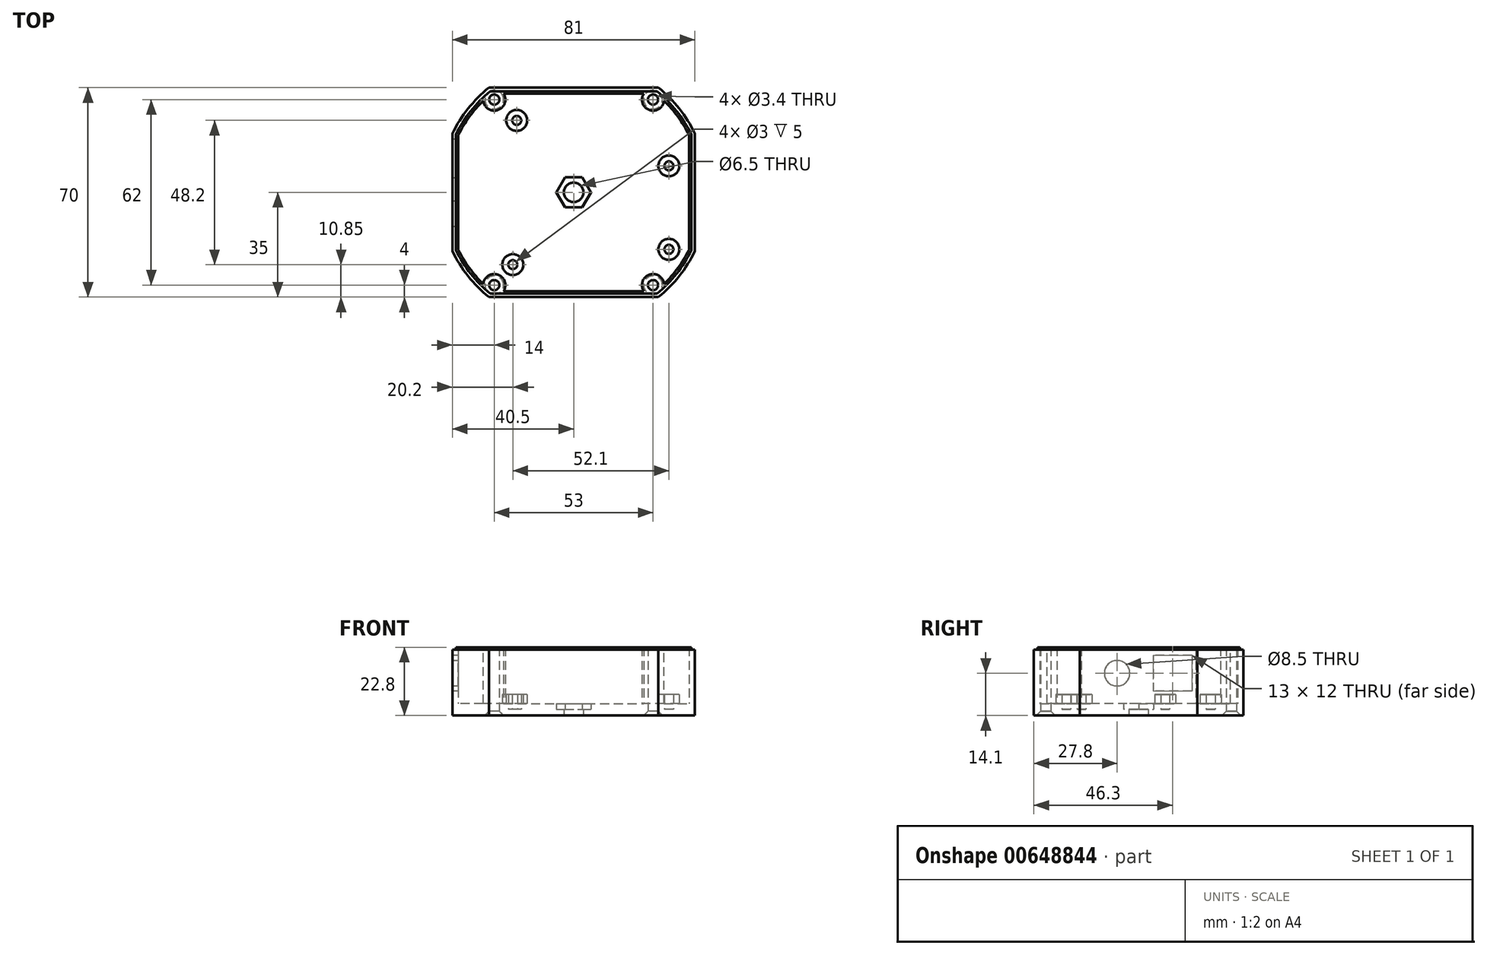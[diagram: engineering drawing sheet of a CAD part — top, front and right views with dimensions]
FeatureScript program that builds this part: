
annotation { "Feature Type Name" : "Feature", "Feature Type Description" : "" }
export const myFeature = defineFeature(function(context is Context, id is Id, definition is map)
    precondition{}
    {
        {
            var Q0;
            Q0=qCreatedBy(makeId("Top.planeOp"),FACE);
            var sketch = newSketch(context, id + "F0", { "sketchPlane" : qUnion([Q0])});
            skArc(sketch, "E0", {"start": v(-40.5, -19.62) * mm, "mid": v(-35.24, -27.98) * mm, "end": v(-28.28, -35) * mm});
            skLineSegment(sketch, "E1", {"start": v(-40.5, 19.62) * mm, "end": v(-40.5, -19.62) * mm});
            skLineSegment(sketch, "E2", {"start": v(-28.28, -35) * mm, "end": v(28.28, -35) * mm});
            skLineSegment(sketch, "E3", {"start": v(-28.28, 35) * mm, "end": v(28.28, 35) * mm});
            skArc(sketch, "E4.trimOffspring", {"start": v(-28.28, 35) * mm, "mid": v(-35.24, 27.98) * mm, "end": v(-40.5, 19.62) * mm});
            skArc(sketch, "E5.trimOffspring", {"start": v(28.28, -35) * mm, "mid": v(35.24, -27.98) * mm, "end": v(40.5, -19.62) * mm});
            skLineSegment(sketch, "E6", {"start": v(40.5, 19.62) * mm, "end": v(40.5, -19.62) * mm});
            skArc(sketch, "E7.trimOffspring", {"start": v(40.5, 19.62) * mm, "mid": v(35.24, 27.98) * mm, "end": v(28.28, 35) * mm});
            skLineSegment(sketch, "E8.bottom", {"start": v(34.3, 26.65) * mm, "end": v(-34.3, 26.65) * mm, "construction": true});
            skLineSegment(sketch, "E8.top", {"start": v(34.3, -26.65) * mm, "end": v(-34.3, -26.65) * mm, "construction": true});
            skLineSegment(sketch, "E8.left", {"start": v(34.3, 26.65) * mm, "end": v(34.3, -26.65) * mm, "construction": true});
            skLineSegment(sketch, "E8.right", {"start": v(-34.3, 26.65) * mm, "end": v(-34.3, -26.65) * mm, "construction": true});
            skLineSegment(sketch, "E9.bottom", {"start": v(-40.5, 17.05) * mm, "end": v(-34.3, 17.05) * mm, "construction": true});
            skLineSegment(sketch, "E9.top", {"start": v(-40.5, 5.05) * mm, "end": v(-34.3, 5.05) * mm, "construction": true});
            skLineSegment(sketch, "E9.left", {"start": v(-40.5, 17.05) * mm, "end": v(-40.5, 5.05) * mm, "construction": true});
            skLineSegment(sketch, "E9.right", {"start": v(-34.3, 17.05) * mm, "end": v(-34.3, 5.05) * mm, "construction": true});
            skPoint(sketch, "E10", {"position": v(-26.5, 31) * mm});
            skPoint(sketch, "E11", {"position": v(26.5, 31) * mm});
            skPoint(sketch, "E12", {"position": v(-26.5, -31) * mm});
            skPoint(sketch, "E13", {"position": v(26.5, -31) * mm});
            skCircle(sketch, "E14", {"center": v(-26.5, 31) * mm, "radius": 1.7 * mm});
            skCircle(sketch, "E15", {"center": v(26.5, 31) * mm, "radius": 1.7 * mm});
            skCircle(sketch, "E16", {"center": v(26.5, -31) * mm, "radius": 1.7 * mm});
            skCircle(sketch, "E17", {"center": v(-26.5, -31) * mm, "radius": 1.7 * mm});
            skPoint(sketch, "E18", {"position": v(-19, 24.05) * mm});
            skPoint(sketch, "E19", {"position": v(31.8, 8.85) * mm});
            skPoint(sketch, "E20", {"position": v(-20.3, -24.15) * mm});
            skPoint(sketch, "E21", {"position": v(31.8, -19.05) * mm});
            skSolve(sketch);
        }
        {
            var Q0;
            Q0=makeQuery(id+"F0.imprint","IMPRINT",FACE,{"disambiguationData":[TD([[makeQuery(id+"F0.imprint","IMPRINT",EDGE,{"derivedFrom":sQuery(id+"F0.wireOp",EDGE,"E0")}),1.0]])]});
            extrude(context, id + "F1", {"entities" : qUnion([Q0]), "depth" : 22 * mm, "offsetDistance" : 25 * mm});
        }
        {
            var Q0;
            Q0=makeQuery(id+"F1.opExtrude","CAP_FACE",FACE,{"disambiguationData":[OSD([sQuery(id+"F0.wireOp",EDGE,"E0"),sQuery(id+"F0.wireOp",EDGE,"E1"),sQuery(id+"F0.wireOp",EDGE,"E2"),sQuery(id+"F0.wireOp",EDGE,"E3"),sQuery(id+"F0.wireOp",EDGE,"E4.trimOffspring"),sQuery(id+"F0.wireOp",EDGE,"E5.trimOffspring"),sQuery(id+"F0.wireOp",EDGE,"E6"),sQuery(id+"F0.wireOp",EDGE,"E7.trimOffspring")])],"isStart":false});
            shell(context, id + "F2", {"entities" : qUnion([Q0]), "thickness" : 2 * mm});
        }
        {
            var Q0;
            Q0=makeQuery(id+"F1.opExtrude","CAP_EDGE",EDGE,{"disambiguationData":[OSD([sQuery(id+"F0.wireOp",EDGE,"E17")])],"isStart":true});
            var Q1;
            Q1=makeQuery(id+"F1.opExtrude","CAP_EDGE",EDGE,{"disambiguationData":[OSD([sQuery(id+"F0.wireOp",EDGE,"E16")])],"isStart":true});
            var Q2;
            Q2=makeQuery(id+"F1.opExtrude","CAP_EDGE",EDGE,{"disambiguationData":[OSD([sQuery(id+"F0.wireOp",EDGE,"E15")])],"isStart":true});
            var Q3;
            Q3=makeQuery(id+"F1.opExtrude","CAP_EDGE",EDGE,{"disambiguationData":[OSD([sQuery(id+"F0.wireOp",EDGE,"E14")])],"isStart":true});
            chamfer(context, id + "F3", {"entities" : qUnion([Q0, Q1, Q2, Q3]), "width" : 1.4 * mm, "tangentPropagation" : true});
        }
        {
            var Q0;
            Q0=makeQuery(id+"F1.opExtrude","CAP_FACE",FACE,{"disambiguationData":[OSD([sQuery(id+"F0.wireOp",EDGE,"E0"),sQuery(id+"F0.wireOp",EDGE,"E1"),sQuery(id+"F0.wireOp",EDGE,"E2"),sQuery(id+"F0.wireOp",EDGE,"E3"),sQuery(id+"F0.wireOp",EDGE,"E4.trimOffspring"),sQuery(id+"F0.wireOp",EDGE,"E5.trimOffspring"),sQuery(id+"F0.wireOp",EDGE,"E6"),sQuery(id+"F0.wireOp",EDGE,"E7.trimOffspring"),sQuery(id+"F0.wireOp",EDGE,"E14"),sQuery(id+"F0.wireOp",EDGE,"E15"),sQuery(id+"F0.wireOp",EDGE,"E16"),sQuery(id+"F0.wireOp",EDGE,"E17")])],"isStart":false});
            var sketch = newSketch(context, id + "F4", { "sketchPlane" : qUnion([Q0])});
            skLineSegment(sketch, "E22.0", {"start": v(-27.86, 33.8) * mm, "end": v(27.86, 33.8) * mm});
            skArc(sketch, "E22.1", {"start": v(39.3, 19.34) * mm, "mid": v(34.35, 27.18) * mm, "end": v(27.86, 33.8) * mm});
            skArc(sketch, "E22.2", {"start": v(-27.86, 33.8) * mm, "mid": v(-34.35, 27.18) * mm, "end": v(-39.3, 19.34) * mm});
            skLineSegment(sketch, "E22.3", {"start": v(39.3, 19.34) * mm, "end": v(39.3, -19.34) * mm});
            skLineSegment(sketch, "E22.4", {"start": v(-39.3, 19.34) * mm, "end": v(-39.3, -19.34) * mm});
            skArc(sketch, "E22.5", {"start": v(-39.3, -19.34) * mm, "mid": v(-34.35, -27.18) * mm, "end": v(-27.86, -33.8) * mm});
            skLineSegment(sketch, "E22.6", {"start": v(-27.86, -33.8) * mm, "end": v(27.86, -33.8) * mm});
            skArc(sketch, "E22.7", {"start": v(27.86, -33.8) * mm, "mid": v(34.35, -27.18) * mm, "end": v(39.3, -19.34) * mm});
            skSolve(sketch);
        }
        {
            var Q0;
            Q0=makeQuery(id+"F4.imprint","IMPRINT",FACE,{"disambiguationData":[TD([[makeQuery(id+"F4.imprint","IMPRINT",EDGE,{"derivedFrom":sQuery(id+"F4.wireOp",EDGE,"E22.0")}),-1.0]])]});
            extrude(context, id + "F5", {"entities" : qUnion([Q0]), "operationType" : NewBodyOperationType.ADD, "depth" : 0.8 * mm, "offsetDistance" : 25 * mm});
        }
        {
            var Q0;
            Q0=makeQuery(id+"F2.opShell","OFFSET_FACE",FACE,{"disambiguationData":[OSD([sQuery(id+"F0.wireOp",EDGE,"E0"),sQuery(id+"F0.wireOp",EDGE,"E1"),sQuery(id+"F0.wireOp",EDGE,"E2"),sQuery(id+"F0.wireOp",EDGE,"E3"),sQuery(id+"F0.wireOp",EDGE,"E4.trimOffspring"),sQuery(id+"F0.wireOp",EDGE,"E5.trimOffspring"),sQuery(id+"F0.wireOp",EDGE,"E6"),sQuery(id+"F0.wireOp",EDGE,"E7.trimOffspring"),sQuery(id+"F0.wireOp",EDGE,"E14"),sQuery(id+"F0.wireOp",EDGE,"E15"),sQuery(id+"F0.wireOp",EDGE,"E16"),sQuery(id+"F0.wireOp",EDGE,"E17")])]});
            var sketch = newSketch(context, id + "F6", { "sketchPlane" : qUnion([Q0])});
            skCircle(sketch, "E23", {"center": v(-19, 24.05) * mm, "radius": 3.5 * mm});
            skCircle(sketch, "E24", {"center": v(31.8, 8.85) * mm, "radius": 3.5 * mm});
            skCircle(sketch, "E25", {"center": v(31.8, -19.05) * mm, "radius": 3.5 * mm});
            skCircle(sketch, "E26", {"center": v(-20.3, -24.15) * mm, "radius": 3.5 * mm});
            skCircle(sketch, "E27", {"center": v(-19, 24.05) * mm, "radius": 1.5 * mm});
            skCircle(sketch, "E28", {"center": v(31.8, 8.85) * mm, "radius": 1.5 * mm});
            skCircle(sketch, "E29", {"center": v(31.8, -19.05) * mm, "radius": 1.5 * mm});
            skCircle(sketch, "E30", {"center": v(-20.3, -24.15) * mm, "radius": 1.5 * mm});
            skSolve(sketch);
        }
        {
            var Q0;
            Q0 = qSketchRegion(id + "F6", true);
            extrude(context, id + "F7", {"entities" : qUnion([Q0]), "operationType" : NewBodyOperationType.ADD, "depth" : 5 * mm, "offsetDistance" : 25 * mm});
        }
        {
            var Q0;
            Q0=makeQuery(id+"F1.opExtrude","SWEPT_FACE",FACE,{"disambiguationData":[OSD([sQuery(id+"F0.wireOp",EDGE,"E1")])]});
            var sketch = newSketch(context, id + "F8", { "sketchPlane" : qUnion([Q0])});
            skLineSegment(sketch, "E31.bottom", {"start": v(-17.8, 20.1) * mm, "end": v(-4.8, 20.1) * mm});
            skLineSegment(sketch, "E31.top", {"start": v(-17.8, 8.1) * mm, "end": v(-4.8, 8.1) * mm});
            skLineSegment(sketch, "E31.left", {"start": v(-17.8, 20.1) * mm, "end": v(-17.8, 8.1) * mm});
            skLineSegment(sketch, "E31.right", {"start": v(-4.8, 20.1) * mm, "end": v(-4.8, 8.1) * mm});
            skCircle(sketch, "E32", {"center": v(7.2, 14.1) * mm, "radius": 4.25 * mm});
            skPoint(sketch, "E33", {"position": v(-4.8, 14.1) * mm});
            skSolve(sketch);
        }
        {
            var Q0;
            Q0=makeQuery(id+"F8.imprint","IMPRINT",FACE,{"disambiguationData":[TD([[makeQuery(id+"F8.imprint","IMPRINT",EDGE,{"derivedFrom":sQuery(id+"F8.wireOp",EDGE,"E31.bottom")}),-1.0]])]});
            var Q1;
            Q1=makeQuery(id+"F8.imprint","IMPRINT",FACE,{"disambiguationData":[TD([[makeQuery(id+"F8.imprint","IMPRINT",EDGE,{"derivedFrom":sQuery(id+"F8.wireOp",EDGE,"E32")}),1.0]])]});
            extrude(context, id + "F9", {"entities" : qUnion([Q0, Q1]), "operationType" : NewBodyOperationType.REMOVE, "endBound" : BoundingType.UP_TO_NEXT, "oppositeDirection" : true, "depth" : 25 * mm, "offsetDistance" : 25 * mm});
        }
        {
            var Q0;
            {var subQ0=sQuery(id+"F0.wireOp",EDGE,"E15");var subQ1=sQuery(id+"F0.wireOp",EDGE,"E14");var subQ2=sQuery(id+"F0.wireOp",EDGE,"E17");var subQ3=sQuery(id+"F0.wireOp",EDGE,"E7.trimOffspring");var subQ4=sQuery(id+"F0.wireOp",EDGE,"E16");var subQ5=sQuery(id+"F0.wireOp",EDGE,"E0");var subQ6=sQuery(id+"F0.wireOp",EDGE,"E3");var subQ7=sQuery(id+"F0.wireOp",EDGE,"E2");var subQ8=sQuery(id+"F0.wireOp",EDGE,"E1");var subQ9=sQuery(id+"F0.wireOp",EDGE,"E4.trimOffspring");var subQ10=sQuery(id+"F0.wireOp",EDGE,"E5.trimOffspring");var subQ11=sQuery(id+"F0.wireOp",EDGE,"E6");Q0=makeQuery(id+"F7.boolean.opBoolean","SPLIT",FACE,{"disambiguationData":[TD([makeQuery(id+"F2.opShell","OFFSET_FACE",FACE,{"disambiguationData":[OSD([subQ5])]})])],"derivedFrom":makeQuery(id+"F2.opShell","OFFSET_FACE",FACE,{"disambiguationData":[OSD([subQ5,subQ8,subQ7,subQ6,subQ9,subQ10,subQ11,subQ3,subQ1,subQ0,subQ4,subQ2])]})});}
            var sketch = newSketch(context, id + "F10", { "sketchPlane" : qUnion([Q0])});
            skCircle(sketch, "E34.cCircle", {"center": v(0, 0) * mm, "radius": 5 * mm, "construction": true});
            skLineSegment(sketch, "E34.0", {"start": v(-2.89, 5) * mm, "end": v(2.89, 5) * mm});
            skLineSegment(sketch, "E34.1", {"start": v(2.89, 5) * mm, "end": v(5.77, 0) * mm});
            skLineSegment(sketch, "E34.2", {"start": v(5.77, 0) * mm, "end": v(2.89, -5) * mm});
            skLineSegment(sketch, "E34.3", {"start": v(2.89, -5) * mm, "end": v(-2.89, -5) * mm});
            skLineSegment(sketch, "E34.4", {"start": v(-2.89, -5) * mm, "end": v(-5.77, 0) * mm});
            skLineSegment(sketch, "E34.5", {"start": v(-5.77, 0) * mm, "end": v(-2.89, 5) * mm});
            skPoint(sketch, "E34.0.midPoint", {"position": v(0, 5) * mm});
            skPoint(sketch, "E35.endSnap0", {"position": v(38.5, 0) * mm});
            skSolve(sketch);
        }
        {
            var Q0;
            Q0=makeQuery(id+"F10.imprint","IMPRINT",FACE,{"disambiguationData":[TD([[makeQuery(id+"F10.imprint","IMPRINT",EDGE,{"derivedFrom":sQuery(id+"F10.wireOp",EDGE,"RWwABV0R-mOg0-w9Vq-6vqf-TQnLn5Bu6DvD")}),1.0]])]});
            var Q1;
            Q1=makeQuery(id+"F10.imprint","IMPRINT",FACE,{"disambiguationData":[TD([[makeQuery(id+"F10.imprint","IMPRINT",EDGE,{"derivedFrom":sQuery(id+"F10.wireOp",EDGE,"E34.0")}),1.0]])]});
            extrude(context, id + "F11", {"entities" : qUnion([Q0, Q1]), "operationType" : NewBodyOperationType.ADD, "depth" : 2 * mm, "offsetDistance" : 25 * mm});
        }
        {
            var Q0;
            Q0=sQuery(id+"F10.wireOp",VERTEX,"E34.cCircle.center");
            var Q1;
            Q1=makeQuery(id+"F1.opExtrude","SWEPT_BODY",BODY,{"disambiguationData":[OSD([sQuery(id+"F0.wireOp",EDGE,"E0"),sQuery(id+"F0.wireOp",EDGE,"E1"),sQuery(id+"F0.wireOp",EDGE,"E2"),sQuery(id+"F0.wireOp",EDGE,"E3"),sQuery(id+"F0.wireOp",EDGE,"E4.trimOffspring"),sQuery(id+"F0.wireOp",EDGE,"E5.trimOffspring"),sQuery(id+"F0.wireOp",EDGE,"E6"),sQuery(id+"F0.wireOp",EDGE,"E7.trimOffspring"),sQuery(id+"F0.wireOp",EDGE,"E14"),sQuery(id+"F0.wireOp",EDGE,"E15"),sQuery(id+"F0.wireOp",EDGE,"E16"),sQuery(id+"F0.wireOp",EDGE,"E17")])]});
            hole(context, id + "F12", {"style" : HoleStyle.SIMPLE, "endStyle" : HoleEndStyle.THROUGH, "holeDiameter" : 6.5 * mm, "majorDiameter" : 5 * mm, "tappedDepth" : 12 * mm, "tapClearance" : 3, "locations" : qUnion([Q0]), "scope" : qUnion([Q1])});
        }
    });
